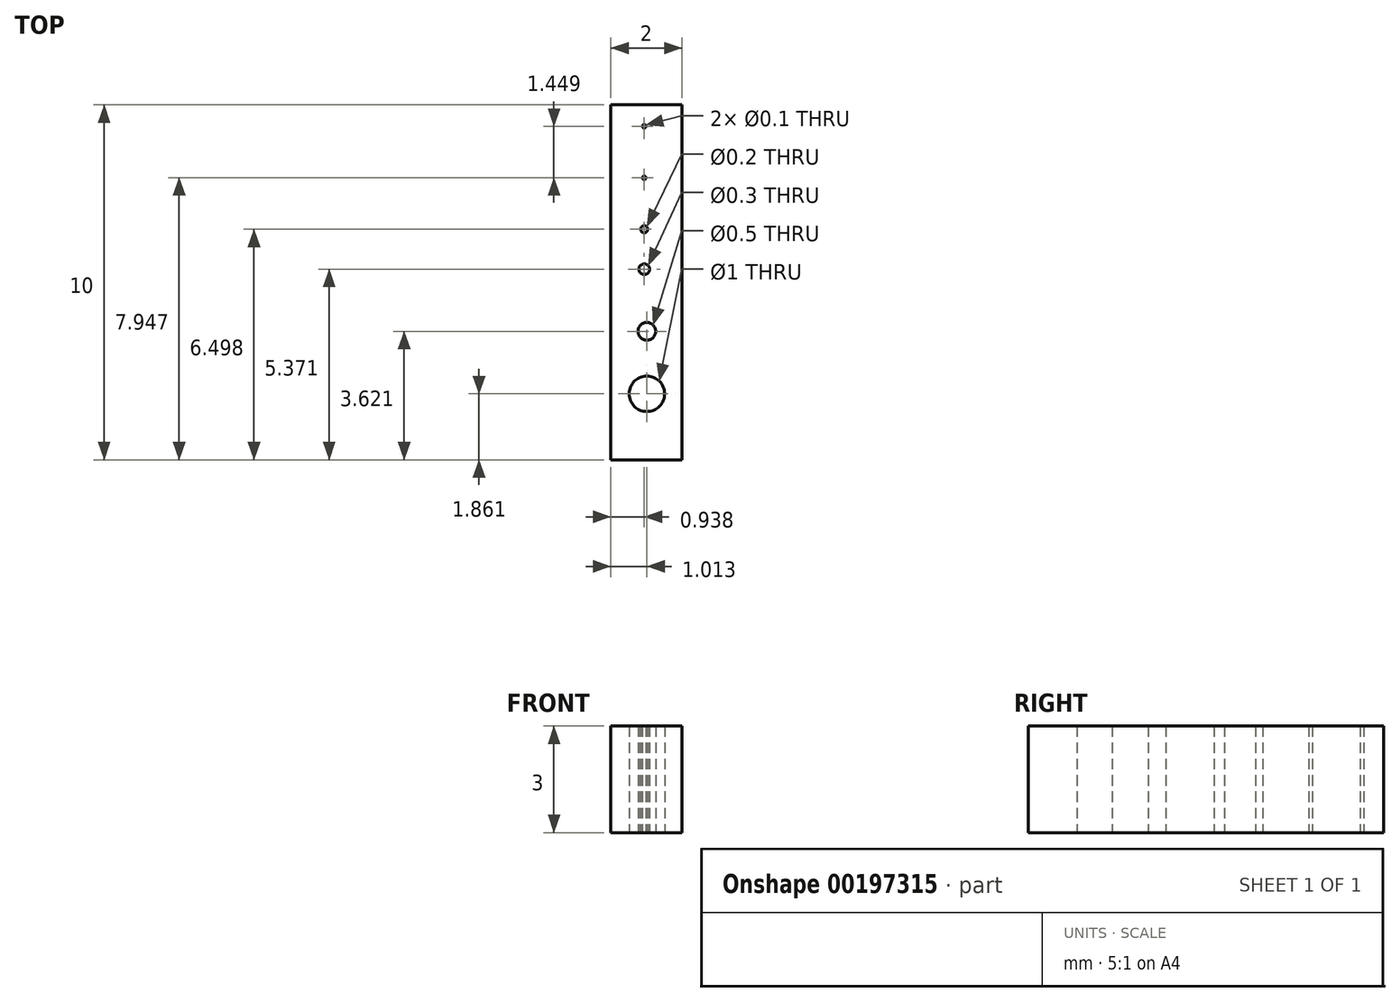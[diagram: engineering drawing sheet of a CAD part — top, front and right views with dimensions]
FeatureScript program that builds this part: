
annotation { "Feature Type Name" : "Feature", "Feature Type Description" : "" }
export const myFeature = defineFeature(function(context is Context, id is Id, definition is map)
    precondition{}
    {
        {
            var Q0;
            Q0=qCreatedBy(makeId("Top.planeOp"),FACE);
            var sketch = newSketch(context, id + "F0", { "sketchPlane" : qUnion([Q0])});
            skLineSegment(sketch, "E0.bottom", {"start": v(0, 0) * mm, "end": v(-2, 0) * mm});
            skLineSegment(sketch, "E0.top", {"start": v(0, 10) * mm, "end": v(-2, 10) * mm});
            skLineSegment(sketch, "E0.left", {"start": v(0, 0) * mm, "end": v(0, 10) * mm});
            skLineSegment(sketch, "E0.right", {"start": v(-2, 0) * mm, "end": v(-2, 10) * mm});
            skCircle(sketch, "E1", {"center": v(-1.06, 9.4) * mm, "radius": 0.05 * mm});
            skCircle(sketch, "E2", {"center": v(-1.06, 7.95) * mm, "radius": 0.05 * mm});
            skCircle(sketch, "E3", {"center": v(-1.06, 6.5) * mm, "radius": 0.1 * mm});
            skCircle(sketch, "E4", {"center": v(-1.06, 5.37) * mm, "radius": 0.15 * mm});
            skCircle(sketch, "E5", {"center": v(-0.99, 3.62) * mm, "radius": 0.25 * mm});
            skCircle(sketch, "E6", {"center": v(-0.99, 1.86) * mm, "radius": 0.5 * mm});
            skSolve(sketch);
        }
        {
            var Q0;
            Q0 = qSketchRegion(id + "F0", true);
            extrude(context, id + "F1", {"entities" : qUnion([Q0]), "depth" : 3 * mm});
        }
    });
